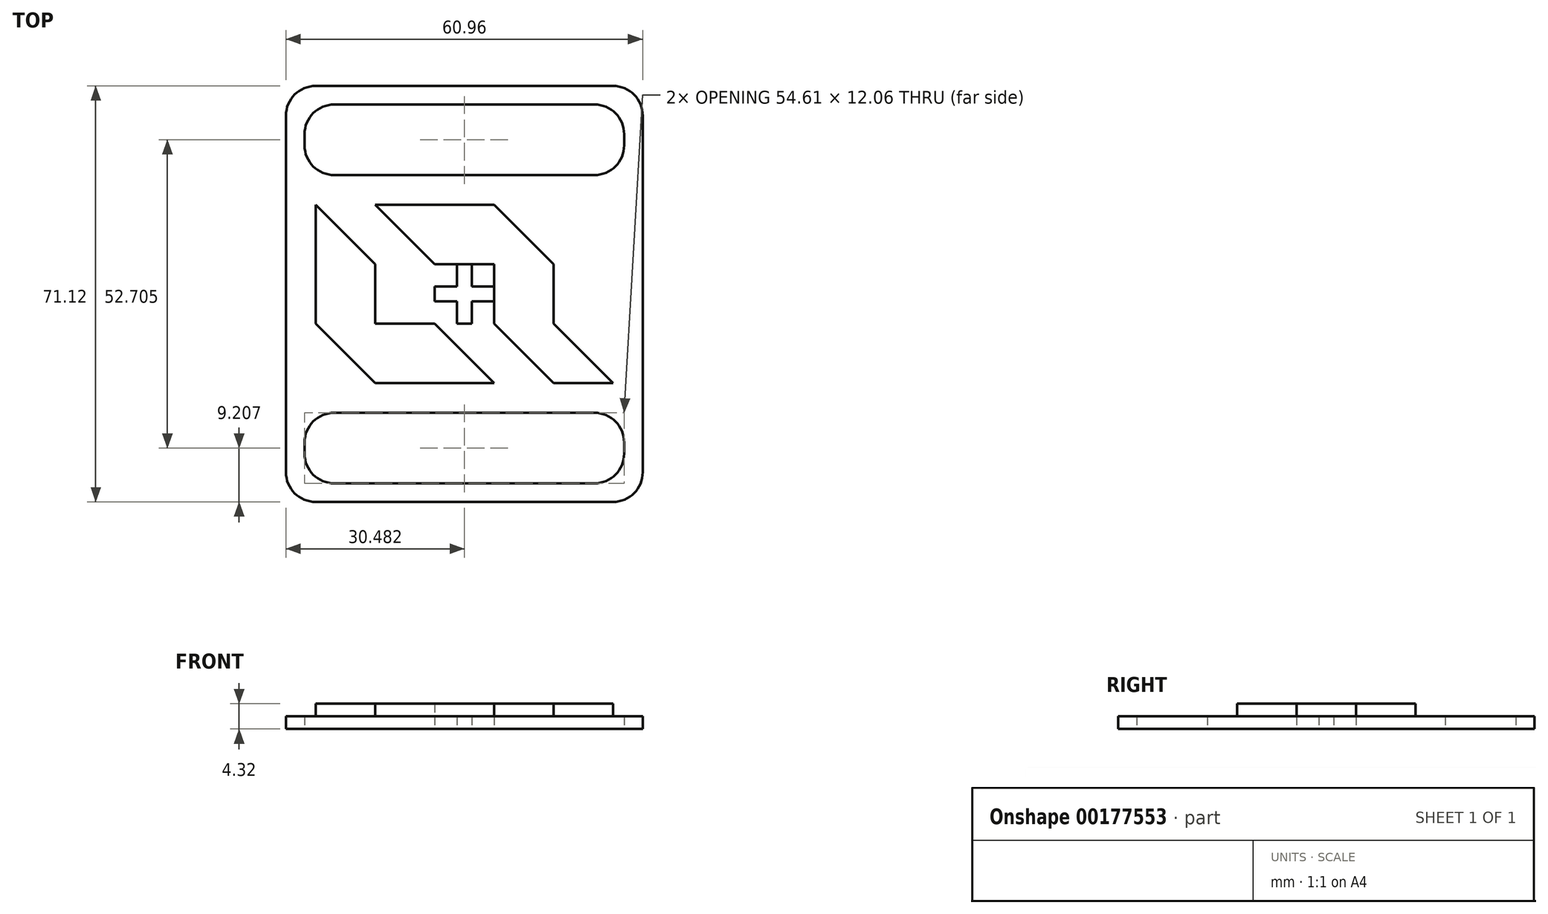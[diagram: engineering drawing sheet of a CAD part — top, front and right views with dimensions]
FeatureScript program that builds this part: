
annotation { "Feature Type Name" : "Feature", "Feature Type Description" : "" }
export const myFeature = defineFeature(function(context is Context, id is Id, definition is map)
    precondition{}
    {
        {
            var Q0;
            Q0=qCreatedBy(makeId("Top.planeOp"),FACE);
            var sketch = newSketch(context, id + "F0", { "sketchPlane" : qUnion([Q0])});
            skLineSegment(sketch, "E0", {"start": v(-20.37, 30.82) * mm, "end": v(-20.37, 20.66) * mm});
            skLineSegment(sketch, "E1", {"start": v(-20.37, 20.66) * mm, "end": v(-10.2, 20.66) * mm});
            skLineSegment(sketch, "E2", {"start": v(-10.2, 20.66) * mm, "end": v(-20.37, 30.82) * mm});
            skLineSegment(sketch, "E3", {"start": v(-10.2, 20.66) * mm, "end": v(-10.2, 0.34) * mm});
            skLineSegment(sketch, "E4", {"start": v(-10.2, 0.34) * mm, "end": v(-20.37, 10.5) * mm});
            skLineSegment(sketch, "E5", {"start": v(-20.37, 10.5) * mm, "end": v(-20.37, 20.66) * mm});
            skLineSegment(sketch, "E6", {"start": v(-10.2, 20.66) * mm, "end": v(-20.37, 10.5) * mm});
            skLineSegment(sketch, "E7", {"start": v(-20.37, 10.5) * mm, "end": v(-10.2, 10.5) * mm});
            skLineSegment(sketch, "E8", {"start": v(-10.2, 10.5) * mm, "end": v(-0.05, 10.5) * mm});
            skLineSegment(sketch, "E9", {"start": v(-0.05, 10.5) * mm, "end": v(10.11, 0.34) * mm});
            skLineSegment(sketch, "E10", {"start": v(10.11, 0.34) * mm, "end": v(-10.2, 0.34) * mm});
            skLineSegment(sketch, "E11", {"start": v(10.11, 0.34) * mm, "end": v(20.27, 0.34) * mm, "construction": true});
            skLineSegment(sketch, "E12", {"start": v(-10.2, 30.82) * mm, "end": v(10.11, 30.82) * mm});
            skLineSegment(sketch, "E13", {"start": v(10.11, 30.82) * mm, "end": v(20.27, 20.66) * mm});
            skLineSegment(sketch, "E14", {"start": v(20.27, 20.66) * mm, "end": v(10.11, 20.66) * mm});
            skLineSegment(sketch, "E15", {"start": v(20.27, 20.66) * mm, "end": v(20.27, 10.5) * mm});
            skLineSegment(sketch, "E16", {"start": v(20.27, 10.5) * mm, "end": v(30.43, 0.34) * mm});
            skLineSegment(sketch, "E17", {"start": v(30.43, 0.34) * mm, "end": v(20.27, 0.34) * mm});
            skLineSegment(sketch, "E18", {"start": v(20.27, 0.34) * mm, "end": v(10.11, 10.5) * mm});
            skLineSegment(sketch, "E19", {"start": v(10.11, 10.5) * mm, "end": v(10.11, 20.66) * mm});
            skLineSegment(sketch, "E20", {"start": v(10.11, 20.66) * mm, "end": v(-0.05, 20.66) * mm});
            skLineSegment(sketch, "E21", {"start": v(-0.05, 20.66) * mm, "end": v(-10.2, 30.82) * mm});
            skLineSegment(sketch, "E22", {"start": v(-0.05, 20.66) * mm, "end": v(-0.05, 30.82) * mm});
            skLineSegment(sketch, "E23", {"start": v(-0.05, 30.82) * mm, "end": v(10.11, 20.66) * mm});
            skLineSegment(sketch, "E24", {"start": v(10.11, 30.82) * mm, "end": v(10.11, 20.66) * mm});
            skLineSegment(sketch, "E25.bottom", {"start": v(35.51, 51.14) * mm, "end": v(-25.45, 51.14) * mm});
            skLineSegment(sketch, "E25.top", {"start": v(35.51, -19.98) * mm, "end": v(-25.45, -19.98) * mm});
            skLineSegment(sketch, "E25.left", {"start": v(35.51, 51.14) * mm, "end": v(35.51, -19.98) * mm});
            skLineSegment(sketch, "E25.right", {"start": v(-25.45, 51.14) * mm, "end": v(-25.45, -19.98) * mm});
            skPoint(sketch, "E25.middle", {"position": v(5.03, 15.58) * mm});
            skPoint(sketch, "E25.middle.positionSnap0", {"position": v(10.11, 15.58) * mm});
            skPoint(sketch, "E25.middle.positionSnap1", {"position": v(5.03, 5.42) * mm});
            skPoint(sketch, "E25.centerSnap0", {"position": v(10.11, 15.58) * mm});
            skPoint(sketch, "E25.centerSnap1", {"position": v(5.03, 5.42) * mm});
            skPoint(sketch, "E26.middle", {"position": v(5.03, -10.77) * mm});
            skPoint(sketch, "E27.middle", {"position": v(5.03, 41.93) * mm});
            skPoint(sketch, "E27.middle.positionSnap0", {"position": v(5.03, 20.66) * mm});
            skPoint(sketch, "E27.centerSnap0", {"position": v(5.03, 20.66) * mm});
            skLineSegment(sketch, "E28.bottom", {"start": v(32.34, -4.74) * mm, "end": v(-22.27, -4.74) * mm});
            skLineSegment(sketch, "E28.top", {"start": v(32.34, -16.8) * mm, "end": v(-22.27, -16.8) * mm});
            skLineSegment(sketch, "E28.left", {"start": v(32.34, -4.74) * mm, "end": v(32.34, -16.8) * mm});
            skLineSegment(sketch, "E28.right", {"start": v(-22.27, -4.74) * mm, "end": v(-22.27, -16.8) * mm});
            skLineSegment(sketch, "E29.bottom", {"start": v(32.34, 47.96) * mm, "end": v(-22.27, 47.96) * mm});
            skLineSegment(sketch, "E29.top", {"start": v(32.34, 35.9) * mm, "end": v(-22.27, 35.9) * mm});
            skLineSegment(sketch, "E29.left", {"start": v(32.34, 47.96) * mm, "end": v(32.34, 35.9) * mm});
            skLineSegment(sketch, "E29.right", {"start": v(-22.27, 47.96) * mm, "end": v(-22.27, 35.9) * mm});
            skLineSegment(sketch, "E30.bottom", {"start": v(10.11, 14.3) * mm, "end": v(-0.05, 14.3) * mm});
            skLineSegment(sketch, "E30.top", {"start": v(10.11, 16.85) * mm, "end": v(-0.05, 16.85) * mm});
            skLineSegment(sketch, "E30.left", {"start": v(10.11, 14.3) * mm, "end": v(10.11, 16.85) * mm});
            skLineSegment(sketch, "E30.right", {"start": v(-0.05, 14.3) * mm, "end": v(-0.05, 16.85) * mm});
            skLineSegment(sketch, "E31.bottom", {"start": v(6.3, 20.66) * mm, "end": v(3.76, 20.66) * mm});
            skLineSegment(sketch, "E31.top", {"start": v(6.3, 10.5) * mm, "end": v(3.76, 10.5) * mm});
            skLineSegment(sketch, "E31.left", {"start": v(6.3, 20.66) * mm, "end": v(6.3, 10.5) * mm});
            skLineSegment(sketch, "E31.right", {"start": v(3.76, 20.66) * mm, "end": v(3.76, 10.5) * mm});
            skSolve(sketch);
        }
        {
            var Q0;
            Q0=makeQuery(id+"F0.imprint","IMPRINT",FACE,{"disambiguationData":[TD([[makeQuery(id+"F0.imprint","IMPRINT",EDGE,{"derivedFrom":sQuery(id+"F0.wireOp",EDGE,"E0")}),1.0]])]});
            var Q1;
            Q1=makeQuery(id+"F0.imprint","IMPRINT",FACE,{"disambiguationData":[TD([[makeQuery(id+"F0.imprint","IMPRINT",EDGE,{"derivedFrom":sQuery(id+"F0.wireOp",EDGE,"E1")}),-1.0]])]});
            var Q2;
            {var subQ0=sQuery(id+"F0.wireOp",EDGE,"E6");Q2=makeQuery(id+"F0.imprint","IMPRINT",FACE,{"disambiguationData":[TD([[makeQuery(id+"F0.imprint","IMPRINT",EDGE,{"derivedFrom":subQ0}),1.0]])]});}
            var Q3;
            {var subQ0=sQuery(id+"F0.wireOp",EDGE,"E4");Q3=makeQuery(id+"F0.imprint","IMPRINT",FACE,{"disambiguationData":[TD([[makeQuery(id+"F0.imprint","IMPRINT",EDGE,{"derivedFrom":subQ0}),-1.0]])]});}
            var Q4;
            {var subQ0=sQuery(id+"F0.wireOp",EDGE,"E21");Q4=makeQuery(id+"F0.imprint","IMPRINT",FACE,{"disambiguationData":[TD([[makeQuery(id+"F0.imprint","IMPRINT",EDGE,{"derivedFrom":subQ0}),-1.0]])]});}
            var Q5;
            Q5=makeQuery(id+"F0.imprint","IMPRINT",FACE,{"disambiguationData":[TD([[makeQuery(id+"F0.imprint","IMPRINT",EDGE,{"derivedFrom":sQuery(id+"F0.wireOp",EDGE,"E20")}),-1.0]])]});
            var Q6;
            {var subQ2=sQuery(id+"F0.wireOp",EDGE,"E23");Q6=makeQuery(id+"F0.imprint","IMPRINT",FACE,{"disambiguationData":[TD([[makeQuery(id+"F0.imprint","IMPRINT",EDGE,{"derivedFrom":subQ2}),1.0]])]});}
            var Q7;
            Q7=makeQuery(id+"F0.imprint","IMPRINT",FACE,{"disambiguationData":[TD([[makeQuery(id+"F0.imprint","IMPRINT",EDGE,{"derivedFrom":sQuery(id+"F0.wireOp",EDGE,"E13")}),-1.0]])]});
            var Q8;
            Q8=makeQuery(id+"F0.imprint","IMPRINT",FACE,{"disambiguationData":[TD([[makeQuery(id+"F0.imprint","IMPRINT",EDGE,{"derivedFrom":sQuery(id+"F0.wireOp",EDGE,"E14")}),1.0]])]});
            var Q9;
            {var subQ2=sQuery(id+"F0.wireOp",EDGE,"E8");Q9=makeQuery(id+"F0.imprint","IMPRINT",FACE,{"disambiguationData":[TD([[makeQuery(id+"F0.imprint","IMPRINT",EDGE,{"derivedFrom":subQ2}),-1.0]])]});}
            extrude(context, id + "F1", {"entities" : qUnion([Q0, Q1, Q2, Q3, Q4, Q5, Q6, Q7, Q8, Q9]), "depth" : 4.32 * mm});
        }
        {
            var Q0;
            Q0=makeQuery(id+"F0.imprint","IMPRINT",FACE,{"disambiguationData":[TD([[makeQuery(id+"F0.imprint","IMPRINT",EDGE,{"derivedFrom":sQuery(id+"F0.wireOp",EDGE,"E0")}),-1.0]])]});
            var Q1;
            {var subQ3=sQuery(id+"F0.wireOp",EDGE,"E30.top");var subQ5=sQuery(id+"F0.wireOp",EDGE,"E31.left");var subQ7=makeQuery(id+"F0.imprint","INTERSECT",VERTEX,{"derivedFrom":[subQ3,subQ5]});Q1=makeQuery(id+"F0.imprint","IMPRINT",FACE,{"disambiguationData":[TD([[makeQuery(id+"F0.imprint","IMPRINT",EDGE,{"disambiguationData":[TD([[subQ7,1.0]])],"derivedFrom":subQ3}),-1.0]])]});}
            extrude(context, id + "F2", {"entities" : qUnion([Q0, Q1]), "operationType" : NewBodyOperationType.ADD, "depth" : 2.16 * mm});
        }
        {
            var Q0;
            Q0=makeQuery(id+"F2.opExtrude","SWEPT_EDGE",EDGE,{"disambiguationData":[OSD([sQuery(id+"F0.wireOp",EDGE,"E25.top"),sQuery(id+"F0.wireOp",EDGE,"E25.right")])]});
            var Q1;
            Q1=makeQuery(id+"F2.opExtrude","SWEPT_EDGE",EDGE,{"disambiguationData":[OSD([sQuery(id+"F0.wireOp",EDGE,"E25.top"),sQuery(id+"F0.wireOp",EDGE,"E25.left")])]});
            var Q2;
            Q2=makeQuery(id+"F2.opExtrude","SWEPT_EDGE",EDGE,{"disambiguationData":[OSD([sQuery(id+"F0.wireOp",EDGE,"E25.bottom"),sQuery(id+"F0.wireOp",EDGE,"E25.left")])]});
            var Q3;
            Q3=makeQuery(id+"F2.opExtrude","SWEPT_EDGE",EDGE,{"disambiguationData":[OSD([sQuery(id+"F0.wireOp",EDGE,"E25.bottom"),sQuery(id+"F0.wireOp",EDGE,"E25.right")])]});
            var Q4;
            Q4=makeQuery(id+"F2.opExtrude","SWEPT_EDGE",EDGE,{"disambiguationData":[OSD([sQuery(id+"F0.wireOp",EDGE,"E28.top"),sQuery(id+"F0.wireOp",EDGE,"E28.right")])]});
            var Q5;
            Q5=makeQuery(id+"F2.opExtrude","SWEPT_EDGE",EDGE,{"disambiguationData":[OSD([sQuery(id+"F0.wireOp",EDGE,"E28.bottom"),sQuery(id+"F0.wireOp",EDGE,"E28.right")])]});
            var Q6;
            Q6=makeQuery(id+"F2.opExtrude","SWEPT_EDGE",EDGE,{"disambiguationData":[OSD([sQuery(id+"F0.wireOp",EDGE,"E29.bottom"),sQuery(id+"F0.wireOp",EDGE,"E29.right")])]});
            var Q7;
            Q7=makeQuery(id+"F2.opExtrude","SWEPT_EDGE",EDGE,{"disambiguationData":[OSD([sQuery(id+"F0.wireOp",EDGE,"E29.top"),sQuery(id+"F0.wireOp",EDGE,"E29.right")])]});
            var Q8;
            Q8=makeQuery(id+"F2.opExtrude","SWEPT_EDGE",EDGE,{"disambiguationData":[OSD([sQuery(id+"F0.wireOp",EDGE,"E28.top"),sQuery(id+"F0.wireOp",EDGE,"E28.left")])]});
            var Q9;
            Q9=makeQuery(id+"F2.opExtrude","SWEPT_EDGE",EDGE,{"disambiguationData":[OSD([sQuery(id+"F0.wireOp",EDGE,"E29.top"),sQuery(id+"F0.wireOp",EDGE,"E29.left")])]});
            var Q10;
            Q10=makeQuery(id+"F2.opExtrude","SWEPT_EDGE",EDGE,{"disambiguationData":[OSD([sQuery(id+"F0.wireOp",EDGE,"E29.bottom"),sQuery(id+"F0.wireOp",EDGE,"E29.left")])]});
            var Q11;
            Q11=makeQuery(id+"F2.opExtrude","SWEPT_EDGE",EDGE,{"disambiguationData":[OSD([sQuery(id+"F0.wireOp",EDGE,"E28.bottom"),sQuery(id+"F0.wireOp",EDGE,"E28.left")])]});
            fillet(context, id + "F3", {"entities" : qUnion([Q0, Q1, Q2, Q3, Q4, Q5, Q6, Q7, Q8, Q9, Q10, Q11]), "radius" : 5.08 * mm, "tangentPropagation" : true, "allowEdgeOverflow" : false});
        }
    });
